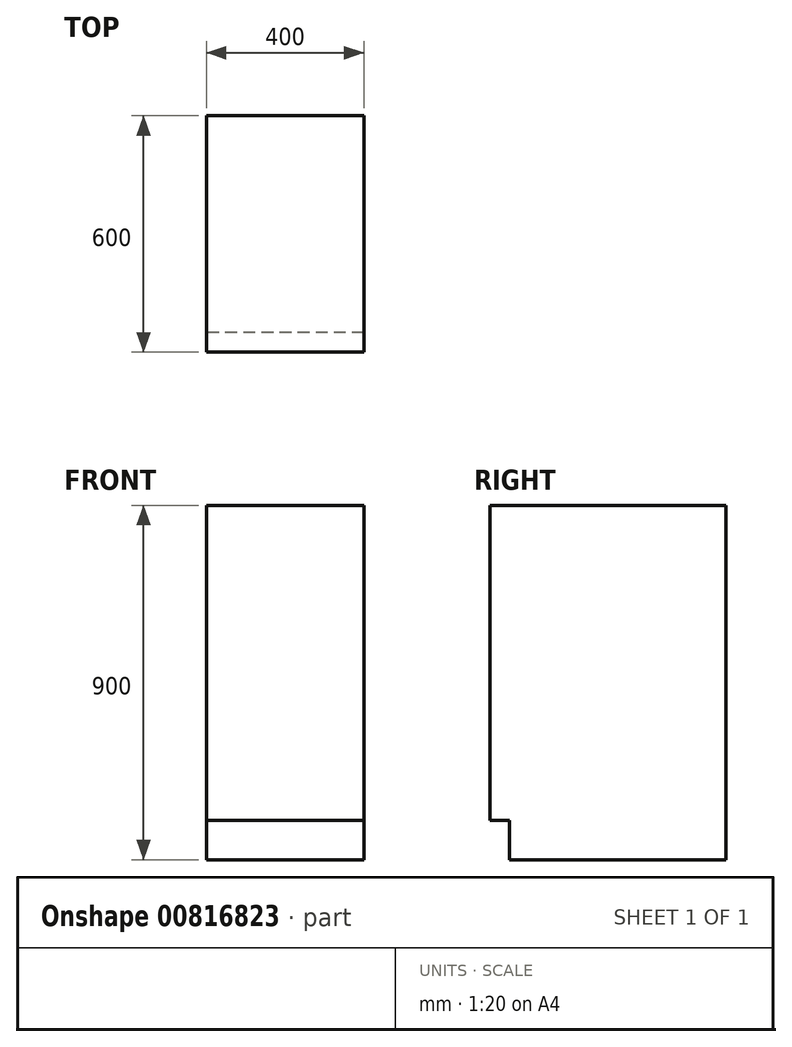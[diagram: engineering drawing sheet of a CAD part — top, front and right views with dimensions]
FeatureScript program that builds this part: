
annotation { "Feature Type Name" : "Feature", "Feature Type Description" : "" }
export const myFeature = defineFeature(function(context is Context, id is Id, definition is map)
    precondition{}
    {
        {
            var Q0;
            Q0=qCreatedBy(makeId("Front.planeOp"),FACE);
            var sketch = newSketch(context, id + "F0", { "sketchPlane" : qUnion([Q0])});
            skLineSegment(sketch, "E0.bottom", {"start": v(0, 0) * mm, "end": v(-400, 0) * mm});
            skLineSegment(sketch, "E0.top", {"start": v(0, 800) * mm, "end": v(-400, 800) * mm});
            skLineSegment(sketch, "E0.left", {"start": v(0, 0) * mm, "end": v(0, 800) * mm});
            skLineSegment(sketch, "E0.right", {"start": v(-400, 0) * mm, "end": v(-400, 800) * mm});
            skSolve(sketch);
        }
        {
            var Q0;
            Q0=makeQuery(id+"F0.imprint","IMPRINT",FACE,{"disambiguationData":[TD([[makeQuery(id+"F0.imprint","IMPRINT",EDGE,{"derivedFrom":sQuery(id+"F0.wireOp",EDGE,"E0.bottom")}),-1.0]])]});
            extrude(context, id + "F1", {"entities" : qUnion([Q0]), "depth" : 600 * mm, "offsetDistance" : 25 * mm});
        }
        {
            var Q0;
            Q0=qCreatedBy(makeId("Front.planeOp"),FACE);
            var sketch = newSketch(context, id + "F2", { "sketchPlane" : qUnion([Q0])});
            skLineSegment(sketch, "E1.bottom", {"start": v(0, 0) * mm, "end": v(-400, 0) * mm});
            skLineSegment(sketch, "E1.top", {"start": v(0, -100) * mm, "end": v(-400, -100) * mm});
            skLineSegment(sketch, "E1.left", {"start": v(0, 0) * mm, "end": v(0, -100) * mm});
            skLineSegment(sketch, "E1.right", {"start": v(-400, 0) * mm, "end": v(-400, -100) * mm});
            skSolve(sketch);
        }
        {
            var Q0;
            Q0 = qSketchRegion(id + "F2", true);
            extrude(context, id + "F3", {"entities" : qUnion([Q0]), "operationType" : NewBodyOperationType.ADD, "depth" : 550 * mm, "offsetDistance" : 25 * mm});
        }
    });
